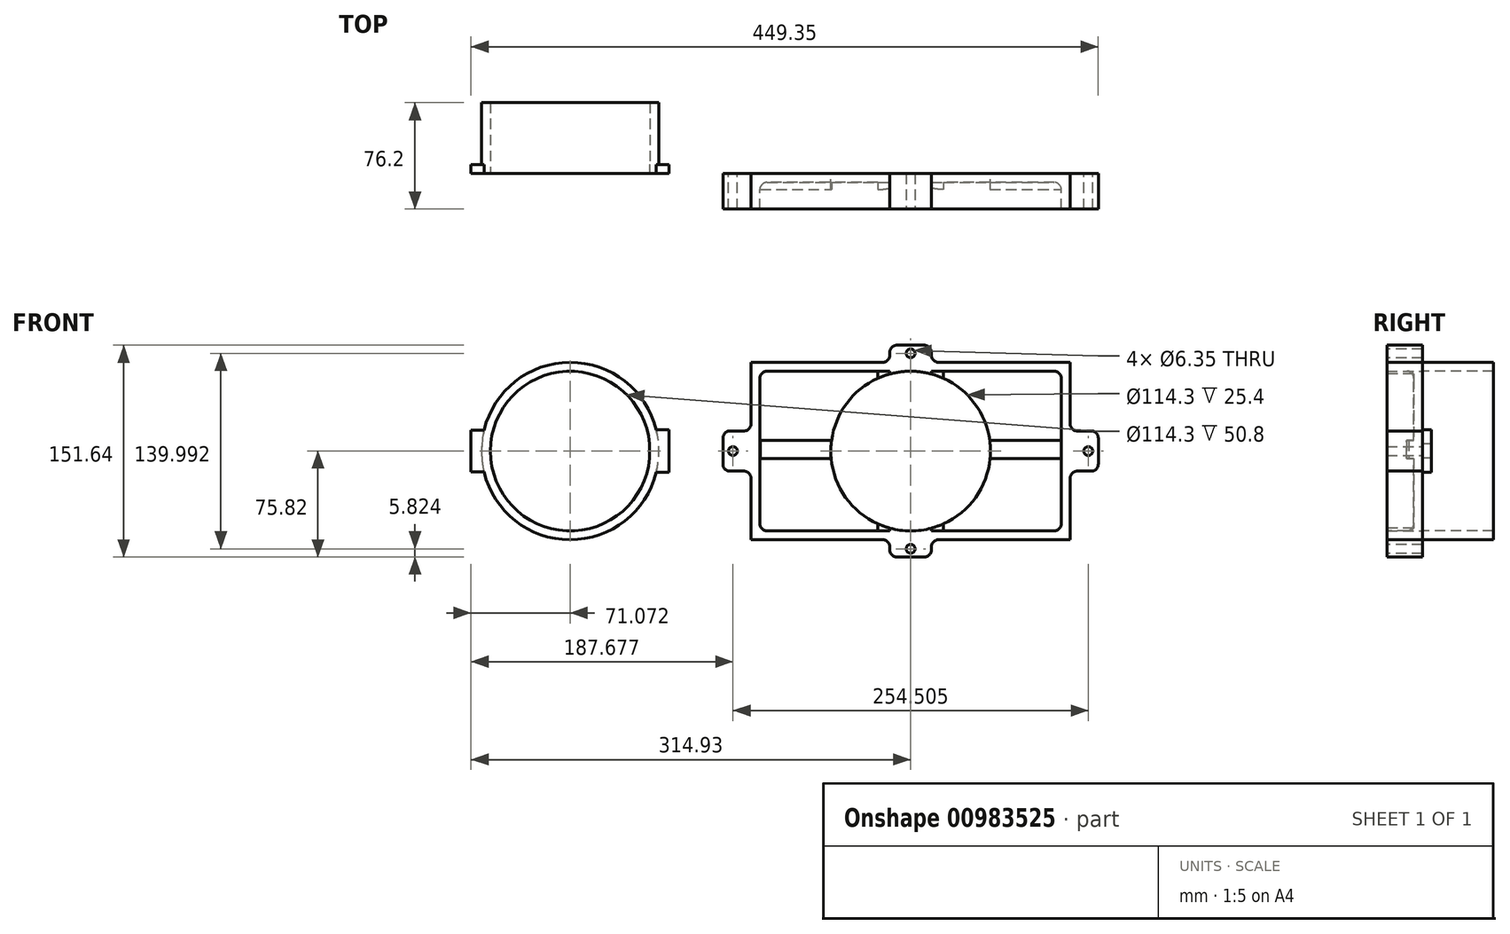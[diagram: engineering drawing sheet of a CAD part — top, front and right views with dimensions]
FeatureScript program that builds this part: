
annotation { "Feature Type Name" : "Feature", "Feature Type Description" : "" }
export const myFeature = defineFeature(function(context is Context, id is Id, definition is map)
    precondition{}
    {
        {
            var Q0;
            Q0=qCreatedBy(makeId("Front.planeOp"),FACE);
            var sketch = newSketch(context, id + "F0", { "sketchPlane" : qUnion([Q0])});
            skLineSegment(sketch, "E0.bottom", {"start": v(114.3, 63.5) * mm, "end": v(-114.3, 63.5) * mm});
            skLineSegment(sketch, "E0.top", {"start": v(114.3, -63.5) * mm, "end": v(-114.3, -63.5) * mm});
            skLineSegment(sketch, "E0.left", {"start": v(114.3, 63.5) * mm, "end": v(114.3, -63.5) * mm});
            skLineSegment(sketch, "E0.right", {"start": v(-114.3, 63.5) * mm, "end": v(-114.3, -63.5) * mm});
            skPoint(sketch, "E0.middle", {"position": v(0, 0) * mm});
            skLineSegment(sketch, "E1.bottom", {"start": v(107.95, 57.15) * mm, "end": v(-107.95, 57.15) * mm});
            skLineSegment(sketch, "E1.top", {"start": v(107.95, -57.15) * mm, "end": v(-107.95, -57.15) * mm});
            skLineSegment(sketch, "E1.left", {"start": v(107.95, 57.15) * mm, "end": v(107.95, -57.15) * mm});
            skLineSegment(sketch, "E1.right", {"start": v(-107.95, 57.15) * mm, "end": v(-107.95, -57.15) * mm});
            skSolve(sketch);
        }
        {
            var Q0;
            Q0 = qSketchRegion(id + "F0", true);
            extrude(context, id + "F1", {"entities" : qUnion([Q0]), "depth" : 25.4 * mm, "offsetDistance" : 25.4 * mm});
        }
        {
            var Q0;
            Q0=qCreatedBy(makeId("Front.planeOp"),FACE);
            var sketch = newSketch(context, id + "F2", { "sketchPlane" : qUnion([Q0])});
            skLineSegment(sketch, "E2.bottom", {"start": v(-114.3, 63.5) * mm, "end": v(114.3, 63.5) * mm});
            skLineSegment(sketch, "E2.top", {"start": v(-114.3, -63.5) * mm, "end": v(114.3, -63.5) * mm});
            skLineSegment(sketch, "E2.left", {"start": v(-114.3, 63.5) * mm, "end": v(-114.3, -63.5) * mm});
            skLineSegment(sketch, "E2.right", {"start": v(114.3, 63.5) * mm, "end": v(114.3, -63.5) * mm});
            skPoint(sketch, "E2.middle", {"position": v(0, 0) * mm});
            skSolve(sketch);
        }
        {
            var Q0;
            Q0 = qSketchRegion(id + "F2", true);
            extrude(context, id + "F3", {"entities" : qUnion([Q0]), "operationType" : NewBodyOperationType.ADD, "depth" : 6.35 * mm, "offsetDistance" : 25.4 * mm});
        }
        {
            var Q0;
            Q0=makeQuery(id+"F3.boolean.opBoolean","MERGE",FACE,{"derivedFrom":[makeQuery(id+"F1.opExtrude","CAP_FACE",FACE,{"disambiguationData":[OSD([sQuery(id+"F0.wireOp",EDGE,"E0.bottom"),sQuery(id+"F0.wireOp",EDGE,"E0.top"),sQuery(id+"F0.wireOp",EDGE,"E0.left"),sQuery(id+"F0.wireOp",EDGE,"E0.right"),sQuery(id+"F0.wireOp",EDGE,"E1.bottom"),sQuery(id+"F0.wireOp",EDGE,"E1.top"),sQuery(id+"F0.wireOp",EDGE,"E1.left"),sQuery(id+"F0.wireOp",EDGE,"E1.right")])],"isStart":true}),makeQuery(id+"F3.opExtrude","CAP_FACE",FACE,{"disambiguationData":[OSD([sQuery(id+"F2.wireOp",EDGE,"E2.bottom"),sQuery(id+"F2.wireOp",EDGE,"E2.top"),sQuery(id+"F2.wireOp",EDGE,"E2.left"),sQuery(id+"F2.wireOp",EDGE,"E2.right")])],"isStart":true})]});
            var sketch = newSketch(context, id + "F4", { "sketchPlane" : qUnion([Q0])});
            skCircle(sketch, "E3", {"center": v(0, 0) * mm, "radius": 57.15 * mm});
            skSolve(sketch);
        }
        {
            var Q0;
            Q0 = qSketchRegion(id + "F4", true);
            extrude(context, id + "F5", {"entities" : qUnion([Q0]), "operationType" : NewBodyOperationType.REMOVE, "oppositeDirection" : true, "depth" : 25.4 * mm, "offsetDistance" : 25.4 * mm});
        }
        {
            var Q0;
            Q0=makeQuery(id+"F1.opExtrude","SWEPT_EDGE",EDGE,{"disambiguationData":[OSD([sQuery(id+"F0.wireOp",EDGE,"E1.top"),sQuery(id+"F0.wireOp",EDGE,"E1.right")])]});
            var Q1;
            Q1=makeQuery(id+"F3.boolean.opBoolean","INTERSECT",EDGE,{"derivedFrom":[makeQuery(id+"F1.opExtrude","SWEPT_FACE",FACE,{"disambiguationData":[OSD([sQuery(id+"F0.wireOp",EDGE,"E1.right")])]}),makeQuery(id+"F3.opExtrude","CAP_FACE",FACE,{"disambiguationData":[OSD([sQuery(id+"F2.wireOp",EDGE,"E2.bottom"),sQuery(id+"F2.wireOp",EDGE,"E2.top"),sQuery(id+"F2.wireOp",EDGE,"E2.left"),sQuery(id+"F2.wireOp",EDGE,"E2.right")])],"isStart":false})]});
            var Q2;
            {var subQ0=makeQuery(id+"F1.opExtrude","SWEPT_FACE",FACE,{"disambiguationData":[OSD([sQuery(id+"F0.wireOp",EDGE,"E1.top")])]});var subQ1=makeQuery(id+"F3.opExtrude","CAP_FACE",FACE,{"disambiguationData":[OSD([sQuery(id+"F2.wireOp",EDGE,"E2.bottom"),sQuery(id+"F2.wireOp",EDGE,"E2.top"),sQuery(id+"F2.wireOp",EDGE,"E2.left"),sQuery(id+"F2.wireOp",EDGE,"E2.right")])],"isStart":false});Q2=makeQuery(id+"F5.boolean.opBoolean","SPLIT",EDGE,{"disambiguationData":[TD([makeQuery(id+"F1.opExtrude","SWEPT_FACE",FACE,{"disambiguationData":[OSD([sQuery(id+"F0.wireOp",EDGE,"E1.right")])]})])],"derivedFrom":makeQuery(id+"F3.boolean.opBoolean","INTERSECT",EDGE,{"derivedFrom":[subQ0,subQ1]})});}
            var Q3;
            Q3=makeQuery(id+"F3.boolean.opBoolean","INTERSECT",EDGE,{"derivedFrom":[makeQuery(id+"F1.opExtrude","SWEPT_FACE",FACE,{"disambiguationData":[OSD([sQuery(id+"F0.wireOp",EDGE,"E1.left")])]}),makeQuery(id+"F3.opExtrude","CAP_FACE",FACE,{"disambiguationData":[OSD([sQuery(id+"F2.wireOp",EDGE,"E2.bottom"),sQuery(id+"F2.wireOp",EDGE,"E2.top"),sQuery(id+"F2.wireOp",EDGE,"E2.left"),sQuery(id+"F2.wireOp",EDGE,"E2.right")])],"isStart":false})]});
            var Q4;
            {var subQ0=makeQuery(id+"F1.opExtrude","SWEPT_FACE",FACE,{"disambiguationData":[OSD([sQuery(id+"F0.wireOp",EDGE,"E1.bottom")])]});var subQ1=makeQuery(id+"F3.opExtrude","CAP_FACE",FACE,{"disambiguationData":[OSD([sQuery(id+"F2.wireOp",EDGE,"E2.bottom"),sQuery(id+"F2.wireOp",EDGE,"E2.top"),sQuery(id+"F2.wireOp",EDGE,"E2.left"),sQuery(id+"F2.wireOp",EDGE,"E2.right")])],"isStart":false});Q4=makeQuery(id+"F5.boolean.opBoolean","SPLIT",EDGE,{"disambiguationData":[TD([makeQuery(id+"F1.opExtrude","SWEPT_FACE",FACE,{"disambiguationData":[OSD([sQuery(id+"F0.wireOp",EDGE,"E1.left")])]})])],"derivedFrom":makeQuery(id+"F3.boolean.opBoolean","INTERSECT",EDGE,{"derivedFrom":[subQ0,subQ1]})});}
            var Q5;
            Q5=makeQuery(id+"F1.opExtrude","SWEPT_EDGE",EDGE,{"disambiguationData":[OSD([sQuery(id+"F0.wireOp",EDGE,"E1.bottom"),sQuery(id+"F0.wireOp",EDGE,"E1.left")])]});
            var Q6;
            Q6=makeQuery(id+"F1.opExtrude","SWEPT_EDGE",EDGE,{"disambiguationData":[OSD([sQuery(id+"F0.wireOp",EDGE,"E1.top"),sQuery(id+"F0.wireOp",EDGE,"E1.left")])]});
            var Q7;
            Q7=makeQuery(id+"F1.opExtrude","SWEPT_EDGE",EDGE,{"disambiguationData":[OSD([sQuery(id+"F0.wireOp",EDGE,"E1.bottom"),sQuery(id+"F0.wireOp",EDGE,"E1.right")])]});
            fillet(context, id + "F6", {"entities" : qUnion([Q0, Q1, Q2, Q3, Q4, Q5, Q6, Q7]), "radius" : 5.08 * mm, "tangentPropagation" : true, "allowEdgeOverflow" : false});
        }
        {
            var Q0;
            Q0=makeQuery(id+"F3.boolean.opBoolean","MERGE",FACE,{"derivedFrom":[makeQuery(id+"F1.opExtrude","CAP_FACE",FACE,{"disambiguationData":[OSD([sQuery(id+"F0.wireOp",EDGE,"E0.bottom"),sQuery(id+"F0.wireOp",EDGE,"E0.top"),sQuery(id+"F0.wireOp",EDGE,"E0.left"),sQuery(id+"F0.wireOp",EDGE,"E0.right"),sQuery(id+"F0.wireOp",EDGE,"E1.bottom"),sQuery(id+"F0.wireOp",EDGE,"E1.top"),sQuery(id+"F0.wireOp",EDGE,"E1.left"),sQuery(id+"F0.wireOp",EDGE,"E1.right")])],"isStart":true}),makeQuery(id+"F3.opExtrude","CAP_FACE",FACE,{"disambiguationData":[OSD([sQuery(id+"F2.wireOp",EDGE,"E2.bottom"),sQuery(id+"F2.wireOp",EDGE,"E2.top"),sQuery(id+"F2.wireOp",EDGE,"E2.left"),sQuery(id+"F2.wireOp",EDGE,"E2.right")])],"isStart":true})]});
            var sketch = newSketch(context, id + "F7", { "sketchPlane" : qUnion([Q0])});
            skCircle(sketch, "E4", {"center": v(243.86, 0) * mm, "radius": 57.15 * mm});
            skCircle(sketch, "E5", {"center": v(243.86, 0) * mm, "radius": 63.5 * mm});
            skSolve(sketch);
        }
        {
            var Q0;
            Q0 = qSketchRegion(id + "F7", true);
            extrude(context, id + "F8", {"entities" : qUnion([Q0]), "depth" : 50.8 * mm, "offsetDistance" : 25.4 * mm});
        }
        {
            var Q0;
            Q0=makeQuery(id+"F3.boolean.opBoolean","MERGE",FACE,{"derivedFrom":[makeQuery(id+"F1.opExtrude","CAP_FACE",FACE,{"disambiguationData":[OSD([sQuery(id+"F0.wireOp",EDGE,"E0.bottom"),sQuery(id+"F0.wireOp",EDGE,"E0.top"),sQuery(id+"F0.wireOp",EDGE,"E0.left"),sQuery(id+"F0.wireOp",EDGE,"E0.right"),sQuery(id+"F0.wireOp",EDGE,"E1.bottom"),sQuery(id+"F0.wireOp",EDGE,"E1.top"),sQuery(id+"F0.wireOp",EDGE,"E1.left"),sQuery(id+"F0.wireOp",EDGE,"E1.right")])],"isStart":true}),makeQuery(id+"F3.opExtrude","CAP_FACE",FACE,{"disambiguationData":[OSD([sQuery(id+"F2.wireOp",EDGE,"E2.bottom"),sQuery(id+"F2.wireOp",EDGE,"E2.top"),sQuery(id+"F2.wireOp",EDGE,"E2.left"),sQuery(id+"F2.wireOp",EDGE,"E2.right")])],"isStart":true})]});
            var sketch = newSketch(context, id + "F9", { "sketchPlane" : qUnion([Q0])});
            skLineSegment(sketch, "E6.bottom", {"start": v(172.96, 15.32) * mm, "end": v(186.93, 15.32) * mm});
            skLineSegment(sketch, "E6.top", {"start": v(172.96, -15.32) * mm, "end": v(186.93, -15.32) * mm});
            skLineSegment(sketch, "E6.left", {"start": v(172.96, 15.32) * mm, "end": v(172.96, -15.32) * mm});
            skLineSegment(sketch, "E6.right", {"start": v(186.93, 15.32) * mm, "end": v(186.93, -15.32) * mm});
            skPoint(sketch, "E6.middle", {"position": v(179.95, 0) * mm});
            skLineSegment(sketch, "E7.bottom", {"start": v(314.93, 15) * mm, "end": v(301.59, 15) * mm});
            skLineSegment(sketch, "E7.top", {"start": v(314.93, -15) * mm, "end": v(301.59, -15) * mm});
            skLineSegment(sketch, "E7.left", {"start": v(314.93, 15) * mm, "end": v(314.93, -15) * mm});
            skLineSegment(sketch, "E7.right", {"start": v(301.59, 15) * mm, "end": v(301.59, -15) * mm});
            skPoint(sketch, "E7.middle", {"position": v(308.26, 0) * mm});
            skSolve(sketch);
        }
        {
            var Q0;
            Q0 = qSketchRegion(id + "F9", true);
            extrude(context, id + "F10", {"entities" : qUnion([Q0]), "operationType" : NewBodyOperationType.ADD, "depth" : 6.35 * mm, "offsetDistance" : 25.4 * mm});
        }
        {
            var Q0;
            Q0=makeQuery(id+"F1.opExtrude","CAP_FACE",FACE,{"disambiguationData":[OSD([sQuery(id+"F0.wireOp",EDGE,"E0.bottom"),sQuery(id+"F0.wireOp",EDGE,"E0.top"),sQuery(id+"F0.wireOp",EDGE,"E0.left"),sQuery(id+"F0.wireOp",EDGE,"E0.right"),sQuery(id+"F0.wireOp",EDGE,"E1.bottom"),sQuery(id+"F0.wireOp",EDGE,"E1.top"),sQuery(id+"F0.wireOp",EDGE,"E1.left"),sQuery(id+"F0.wireOp",EDGE,"E1.right")])],"isStart":false});
            var sketch = newSketch(context, id + "F11", { "sketchPlane" : qUnion([Q0])});
            skLineSegment(sketch, "E8.bottom", {"start": v(14.94, 75.82) * mm, "end": v(-14.94, 75.82) * mm});
            skLineSegment(sketch, "E8.top", {"start": v(14.94, 51.18) * mm, "end": v(-14.94, 51.18) * mm});
            skLineSegment(sketch, "E8.left", {"start": v(14.94, 75.82) * mm, "end": v(14.94, 51.18) * mm});
            skLineSegment(sketch, "E8.right", {"start": v(-14.94, 75.82) * mm, "end": v(-14.94, 51.18) * mm});
            skPoint(sketch, "E8.middle", {"position": v(0, 63.5) * mm});
            skCircle(sketch, "E9", {"center": v(0, 70) * mm, "radius": 3.18 * mm});
            skLineSegment(sketch, "E10.MirrorCS", {"start": v(14.94, -75.82) * mm, "end": v(14.94, -51.18) * mm});
            skLineSegment(sketch, "E11.MirrorCS", {"start": v(14.94, -75.82) * mm, "end": v(-14.94, -75.82) * mm});
            skLineSegment(sketch, "E12.MirrorCS", {"start": v(-14.94, -75.82) * mm, "end": v(-14.94, -51.18) * mm});
            skLineSegment(sketch, "E13.MirrorCS", {"start": v(14.94, -51.18) * mm, "end": v(-14.94, -51.18) * mm});
            skCircle(sketch, "E14.MirrorC", {"center": v(0, -70) * mm, "radius": 3.18 * mm});
            skSolve(sketch);
        }
        {
            var Q0;
            Q0 = qSketchRegion(id + "F11", true);
            extrude(context, id + "F12", {"entities" : qUnion([Q0]), "operationType" : NewBodyOperationType.ADD, "oppositeDirection" : true, "depth" : 25.4 * mm, "offsetDistance" : 25.4 * mm});
        }
        {
            var Q0;
            Q0=makeQuery(id+"F12.opExtrude","SWEPT_EDGE",EDGE,{"disambiguationData":[OSD([sQuery(id+"F11.wireOp",EDGE,"E8.bottom"),sQuery(id+"F11.wireOp",EDGE,"E8.right")])]});
            var Q1;
            Q1=makeQuery(id+"F12.opExtrude","SWEPT_EDGE",EDGE,{"disambiguationData":[OSD([sQuery(id+"F11.wireOp",EDGE,"E8.bottom"),sQuery(id+"F11.wireOp",EDGE,"E8.left")])]});
            var Q2;
            Q2=makeQuery(id+"F12.boolean.opBoolean","INTERSECT",EDGE,{"derivedFrom":[makeQuery(id+"F1.opExtrude","SWEPT_FACE",FACE,{"disambiguationData":[OSD([sQuery(id+"F0.wireOp",EDGE,"E0.bottom")])]}),makeQuery(id+"F12.opExtrude","SWEPT_FACE",FACE,{"disambiguationData":[OSD([sQuery(id+"F11.wireOp",EDGE,"E8.left")])]})]});
            var Q3;
            Q3=makeQuery(id+"F12.boolean.opBoolean","INTERSECT",EDGE,{"derivedFrom":[makeQuery(id+"F1.opExtrude","SWEPT_FACE",FACE,{"disambiguationData":[OSD([sQuery(id+"F0.wireOp",EDGE,"E0.bottom")])]}),makeQuery(id+"F12.opExtrude","SWEPT_FACE",FACE,{"disambiguationData":[OSD([sQuery(id+"F11.wireOp",EDGE,"E8.right")])]})]});
            fillet(context, id + "F13", {"entities" : qUnion([Q0, Q1, Q2, Q3]), "radius" : 5.08 * mm, "tangentPropagation" : true, "allowEdgeOverflow" : false});
        }
        {
            var Q0;
            Q0=makeQuery(id+"F12.boolean.opBoolean","INTERSECT",EDGE,{"derivedFrom":[makeQuery(id+"F1.opExtrude","SWEPT_FACE",FACE,{"disambiguationData":[OSD([sQuery(id+"F0.wireOp",EDGE,"E0.top")])]}),makeQuery(id+"F12.opExtrude","SWEPT_FACE",FACE,{"disambiguationData":[OSD([sQuery(id+"F11.wireOp",EDGE,"E10.MirrorCS")])]})]});
            var Q1;
            Q1=makeQuery(id+"F12.opExtrude","SWEPT_EDGE",EDGE,{"disambiguationData":[OSD([sQuery(id+"F11.wireOp",EDGE,"E10.MirrorCS"),sQuery(id+"F11.wireOp",EDGE,"E11.MirrorCS")])]});
            var Q2;
            Q2=makeQuery(id+"F12.opExtrude","SWEPT_EDGE",EDGE,{"disambiguationData":[OSD([sQuery(id+"F11.wireOp",EDGE,"E11.MirrorCS"),sQuery(id+"F11.wireOp",EDGE,"E12.MirrorCS")])]});
            var Q3;
            Q3=makeQuery(id+"F12.boolean.opBoolean","INTERSECT",EDGE,{"derivedFrom":[makeQuery(id+"F1.opExtrude","SWEPT_FACE",FACE,{"disambiguationData":[OSD([sQuery(id+"F0.wireOp",EDGE,"E0.top")])]}),makeQuery(id+"F12.opExtrude","SWEPT_FACE",FACE,{"disambiguationData":[OSD([sQuery(id+"F11.wireOp",EDGE,"E12.MirrorCS")])]})]});
            fillet(context, id + "F14", {"entities" : qUnion([Q0, Q1, Q2, Q3]), "radius" : 5.08 * mm, "tangentPropagation" : true, "allowEdgeOverflow" : false});
        }
        {
            var Q0;
            Q0=qCreatedBy(makeId("Front.planeOp"),FACE);
            var sketch = newSketch(context, id + "F15", { "sketchPlane" : qUnion([Q0])});
            skLineSegment(sketch, "E15.bottom", {"start": v(-113.73, 14.39) * mm, "end": v(-134.42, 14.39) * mm});
            skLineSegment(sketch, "E15.top", {"start": v(-113.73, -14.39) * mm, "end": v(-134.42, -14.39) * mm});
            skLineSegment(sketch, "E15.left", {"start": v(-113.73, 14.39) * mm, "end": v(-113.73, -14.39) * mm});
            skLineSegment(sketch, "E15.right", {"start": v(-134.42, 14.39) * mm, "end": v(-134.42, -14.39) * mm});
            skPoint(sketch, "E15.middle", {"position": v(-124.08, 0) * mm});
            skCircle(sketch, "E16", {"center": v(-127.25, 0) * mm, "radius": 3.18 * mm});
            skLineSegment(sketch, "E17.MirrorCS", {"start": v(113.73, 14.39) * mm, "end": v(134.42, 14.39) * mm});
            skLineSegment(sketch, "E18.MirrorCS", {"start": v(134.42, 14.39) * mm, "end": v(134.42, -14.39) * mm});
            skLineSegment(sketch, "E19.MirrorCS", {"start": v(113.73, -14.39) * mm, "end": v(134.42, -14.39) * mm});
            skCircle(sketch, "E20.MirrorC", {"center": v(127.25, 0) * mm, "radius": 3.18 * mm});
            skSolve(sketch);
        }
        {
            var Q0;
            Q0 = qSketchRegion(id + "F15", true);
            extrude(context, id + "F16", {"entities" : qUnion([Q0]), "operationType" : NewBodyOperationType.ADD, "depth" : 25.4 * mm, "offsetDistance" : 25.4 * mm});
        }
        {
            var Q0;
            Q0=makeQuery(id+"F16.boolean.opBoolean","INTERSECT",EDGE,{"derivedFrom":[makeQuery(id+"F1.opExtrude","SWEPT_FACE",FACE,{"disambiguationData":[OSD([sQuery(id+"F0.wireOp",EDGE,"E0.right")])]}),makeQuery(id+"F16.opExtrude","SWEPT_FACE",FACE,{"disambiguationData":[OSD([sQuery(id+"F15.wireOp",EDGE,"E15.bottom")])]})]});
            var Q1;
            Q1=makeQuery(id+"F16.opExtrude","SWEPT_EDGE",EDGE,{"disambiguationData":[OSD([sQuery(id+"F15.wireOp",EDGE,"E15.bottom"),sQuery(id+"F15.wireOp",EDGE,"E15.right")])]});
            var Q2;
            Q2=makeQuery(id+"F16.opExtrude","SWEPT_EDGE",EDGE,{"disambiguationData":[OSD([sQuery(id+"F15.wireOp",EDGE,"E15.top"),sQuery(id+"F15.wireOp",EDGE,"E15.right")])]});
            var Q3;
            Q3=makeQuery(id+"F16.boolean.opBoolean","INTERSECT",EDGE,{"derivedFrom":[makeQuery(id+"F1.opExtrude","SWEPT_FACE",FACE,{"disambiguationData":[OSD([sQuery(id+"F0.wireOp",EDGE,"E0.right")])]}),makeQuery(id+"F16.opExtrude","SWEPT_FACE",FACE,{"disambiguationData":[OSD([sQuery(id+"F15.wireOp",EDGE,"E15.top")])]})]});
            fillet(context, id + "F17", {"entities" : qUnion([Q0, Q1, Q2, Q3]), "radius" : 5.08 * mm, "tangentPropagation" : true, "allowEdgeOverflow" : false});
        }
        {
            var Q0;
            Q0=makeQuery(id+"F1.opExtrude","SWEPT_BODY",BODY,{"disambiguationData":[OSD([sQuery(id+"F0.wireOp",EDGE,"E0.bottom"),sQuery(id+"F0.wireOp",EDGE,"E0.top"),sQuery(id+"F0.wireOp",EDGE,"E0.left"),sQuery(id+"F0.wireOp",EDGE,"E0.right"),sQuery(id+"F0.wireOp",EDGE,"E1.bottom"),sQuery(id+"F0.wireOp",EDGE,"E1.top"),sQuery(id+"F0.wireOp",EDGE,"E1.left"),sQuery(id+"F0.wireOp",EDGE,"E1.right")])]});
            var Q1;
            Q1=qCreatedBy(makeId("Right.planeOp"),FACE);
            mirror(context, id + "F18", {"entities" : qUnion([Q0]), "mirrorPlane" : qUnion([Q1])});
        }
        {
            var Q0;
            Q0=makeQuery(id+"F18.opPattern","COPY",FACE,{"derivedFrom":makeQuery(id+"F16.boolean.opBoolean","MERGE",FACE,{"derivedFrom":[makeQuery(id+"F12.boolean.opBoolean","MERGE",FACE,{"derivedFrom":[makeQuery(id+"F1.opExtrude","CAP_FACE",FACE,{"disambiguationData":[OSD([sQuery(id+"F0.wireOp",EDGE,"E0.bottom"),sQuery(id+"F0.wireOp",EDGE,"E0.top"),sQuery(id+"F0.wireOp",EDGE,"E0.left"),sQuery(id+"F0.wireOp",EDGE,"E0.right"),sQuery(id+"F0.wireOp",EDGE,"E1.bottom"),sQuery(id+"F0.wireOp",EDGE,"E1.top"),sQuery(id+"F0.wireOp",EDGE,"E1.left"),sQuery(id+"F0.wireOp",EDGE,"E1.right")])],"isStart":false}),makeQuery(id+"F12.opExtrude","CAP_FACE",FACE,{"disambiguationData":[OSD([sQuery(id+"F11.wireOp",EDGE,"E8.bottom"),sQuery(id+"F11.wireOp",EDGE,"E8.top"),sQuery(id+"F11.wireOp",EDGE,"E8.left"),sQuery(id+"F11.wireOp",EDGE,"E8.right"),sQuery(id+"F11.wireOp",EDGE,"E9")])],"isStart":true}),makeQuery(id+"F12.opExtrude","CAP_FACE",FACE,{"disambiguationData":[OSD([sQuery(id+"F11.wireOp",EDGE,"E10.MirrorCS"),sQuery(id+"F11.wireOp",EDGE,"E11.MirrorCS"),sQuery(id+"F11.wireOp",EDGE,"E12.MirrorCS"),sQuery(id+"F11.wireOp",EDGE,"E13.MirrorCS"),sQuery(id+"F11.wireOp",EDGE,"E14.MirrorC")])],"isStart":true})]}),makeQuery(id+"F16.opExtrude","CAP_FACE",FACE,{"disambiguationData":[OSD([sQuery(id+"F15.wireOp",EDGE,"E15.bottom"),sQuery(id+"F15.wireOp",EDGE,"E15.top"),sQuery(id+"F15.wireOp",EDGE,"E15.left"),sQuery(id+"F15.wireOp",EDGE,"E15.right"),sQuery(id+"F15.wireOp",EDGE,"E16")])],"isStart":false})]}),"instanceName":"1"});
            var sketch = newSketch(context, id + "F19", { "sketchPlane" : qUnion([Q0])});
            skCircle(sketch, "E21", {"center": v(127.25, 0) * mm, "radius": 3.18 * mm});
            skSolve(sketch);
        }
        {
            var Q0;
            Q0 = qSketchRegion(id + "F19", true);
            extrude(context, id + "F20", {"entities" : qUnion([Q0]), "operationType" : NewBodyOperationType.REMOVE, "oppositeDirection" : true, "depth" : 25.4 * mm, "offsetDistance" : 25.4 * mm});
        }
        {
            var Q0;
            {var subQ0=makeQuery(id+"F3.opExtrude","CAP_FACE",FACE,{"disambiguationData":[OSD([sQuery(id+"F2.wireOp",EDGE,"E2.bottom"),sQuery(id+"F2.wireOp",EDGE,"E2.top"),sQuery(id+"F2.wireOp",EDGE,"E2.left"),sQuery(id+"F2.wireOp",EDGE,"E2.right")])],"isStart":false});Q0=makeQuery(id+"F5.boolean.opBoolean","SPLIT",FACE,{"disambiguationData":[TD([makeQuery(id+"F1.opExtrude","SWEPT_FACE",FACE,{"disambiguationData":[OSD([sQuery(id+"F0.wireOp",EDGE,"E1.right")])]})])],"derivedFrom":subQ0});}
            var sketch = newSketch(context, id + "F21", { "sketchPlane" : qUnion([Q0])});
            skCircle(sketch, "E22", {"center": v(0, 0) * mm, "radius": 57.15 * mm});
            skSolve(sketch);
        }
        {
            var Q0;
            Q0 = qSketchRegion(id + "F21", true);
            extrude(context, id + "F22", {"entities" : qUnion([Q0]), "operationType" : NewBodyOperationType.REMOVE, "endBound" : BoundingType.SYMMETRIC, "oppositeDirection" : true, "depth" : 50.8 * mm, "offsetDistance" : 25.4 * mm});
        }
        {
            var Q0;
            {var subQ0=makeQuery(id+"F3.opExtrude","CAP_FACE",FACE,{"disambiguationData":[OSD([sQuery(id+"F2.wireOp",EDGE,"E2.bottom"),sQuery(id+"F2.wireOp",EDGE,"E2.top"),sQuery(id+"F2.wireOp",EDGE,"E2.left"),sQuery(id+"F2.wireOp",EDGE,"E2.right")])],"isStart":false});Q0=makeQuery(id+"F5.boolean.opBoolean","SPLIT",FACE,{"disambiguationData":[TD([makeQuery(id+"F1.opExtrude","SWEPT_FACE",FACE,{"disambiguationData":[OSD([sQuery(id+"F0.wireOp",EDGE,"E1.right")])]})])],"derivedFrom":subQ0});}
            var sketch = newSketch(context, id + "F23", { "sketchPlane" : qUnion([Q0])});
            skLineSegment(sketch, "E23.bottom", {"start": v(-107.68, -5.25) * mm, "end": v(123.83, -5.25) * mm});
            skLineSegment(sketch, "E23.top", {"start": v(-107.68, 7.62) * mm, "end": v(123.83, 7.62) * mm});
            skLineSegment(sketch, "E23.left", {"start": v(-107.68, -5.25) * mm, "end": v(-107.68, 7.62) * mm});
            skLineSegment(sketch, "E23.right", {"start": v(123.83, -5.25) * mm, "end": v(123.83, 7.62) * mm});
            skSolve(sketch);
        }
        {
            var Q0;
            Q0 = qSketchRegion(id + "F23", true);
            extrude(context, id + "F24", {"entities" : qUnion([Q0]), "operationType" : NewBodyOperationType.ADD, "depth" : 5.08 * mm, "offsetDistance" : 25.4 * mm});
        }
        {
            var Q0;
            Q0=makeQuery(id+"F24.opExtrude","CAP_FACE",FACE,{"disambiguationData":[OSD([sQuery(id+"F23.wireOp",EDGE,"E23.bottom"),sQuery(id+"F23.wireOp",EDGE,"E23.top"),sQuery(id+"F23.wireOp",EDGE,"E23.left"),sQuery(id+"F23.wireOp",EDGE,"E23.right")])],"isStart":false});
            var sketch = newSketch(context, id + "F25", { "sketchPlane" : qUnion([Q0])});
            skCircle(sketch, "E24", {"center": v(0, 0) * mm, "radius": 57.15 * mm});
            skSolve(sketch);
        }
        {
            var Q0;
            Q0 = qSketchRegion(id + "F25", true);
            extrude(context, id + "F26", {"entities" : qUnion([Q0]), "operationType" : NewBodyOperationType.REMOVE, "oppositeDirection" : true, "depth" : 25.4 * mm, "offsetDistance" : 25.4 * mm});
        }
        {
            var Q0;
            {var subQ0=makeQuery(id+"F16.boolean.opBoolean","MERGE",FACE,{"derivedFrom":[makeQuery(id+"F12.boolean.opBoolean","MERGE",FACE,{"derivedFrom":[makeQuery(id+"F3.boolean.opBoolean","MERGE",FACE,{"derivedFrom":[makeQuery(id+"F1.opExtrude","CAP_FACE",FACE,{"disambiguationData":[OSD([sQuery(id+"F0.wireOp",EDGE,"E0.bottom"),sQuery(id+"F0.wireOp",EDGE,"E0.top"),sQuery(id+"F0.wireOp",EDGE,"E0.left"),sQuery(id+"F0.wireOp",EDGE,"E0.right"),sQuery(id+"F0.wireOp",EDGE,"E1.bottom"),sQuery(id+"F0.wireOp",EDGE,"E1.top"),sQuery(id+"F0.wireOp",EDGE,"E1.left"),sQuery(id+"F0.wireOp",EDGE,"E1.right")])],"isStart":true}),makeQuery(id+"F3.opExtrude","CAP_FACE",FACE,{"disambiguationData":[OSD([sQuery(id+"F2.wireOp",EDGE,"E2.bottom"),sQuery(id+"F2.wireOp",EDGE,"E2.top"),sQuery(id+"F2.wireOp",EDGE,"E2.left"),sQuery(id+"F2.wireOp",EDGE,"E2.right")])],"isStart":true})]}),makeQuery(id+"F12.opExtrude","CAP_FACE",FACE,{"disambiguationData":[OSD([sQuery(id+"F11.wireOp",EDGE,"E8.bottom"),sQuery(id+"F11.wireOp",EDGE,"E8.top"),sQuery(id+"F11.wireOp",EDGE,"E8.left"),sQuery(id+"F11.wireOp",EDGE,"E8.right"),sQuery(id+"F11.wireOp",EDGE,"E9")])],"isStart":false}),makeQuery(id+"F12.opExtrude","CAP_FACE",FACE,{"disambiguationData":[OSD([sQuery(id+"F11.wireOp",EDGE,"E10.MirrorCS"),sQuery(id+"F11.wireOp",EDGE,"E11.MirrorCS"),sQuery(id+"F11.wireOp",EDGE,"E12.MirrorCS"),sQuery(id+"F11.wireOp",EDGE,"E13.MirrorCS"),sQuery(id+"F11.wireOp",EDGE,"E14.MirrorC")])],"isStart":false})]}),makeQuery(id+"F16.opExtrude","CAP_FACE",FACE,{"disambiguationData":[OSD([sQuery(id+"F15.wireOp",EDGE,"E15.bottom"),sQuery(id+"F15.wireOp",EDGE,"E15.top"),sQuery(id+"F15.wireOp",EDGE,"E15.left"),sQuery(id+"F15.wireOp",EDGE,"E15.right"),sQuery(id+"F15.wireOp",EDGE,"E16")])],"isStart":true})]});Q0=makeQuery(id+"F24.boolean.opBoolean","MERGE",FACE,{"derivedFrom":[makeQuery(id+"F18.opPattern","COPY",FACE,{"derivedFrom":subQ0,"instanceName":"1"}),subQ0]});}
            var sketch = newSketch(context, id + "F27", { "sketchPlane" : qUnion([Q0])});
            skCircle(sketch, "E25", {"center": v(0, 0) * mm, "radius": 57.15 * mm});
            skSolve(sketch);
        }
        {
            var Q0;
            Q0 = qSketchRegion(id + "F27", true);
            extrude(context, id + "F28", {"entities" : qUnion([Q0]), "operationType" : NewBodyOperationType.REMOVE, "oppositeDirection" : true, "depth" : 25.4 * mm, "offsetDistance" : 25.4 * mm});
        }
    });
